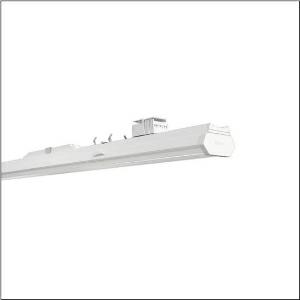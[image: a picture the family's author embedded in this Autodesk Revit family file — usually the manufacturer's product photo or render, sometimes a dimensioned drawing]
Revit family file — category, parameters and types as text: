
# Revit family: licross_r__11_protected_ho_51tp12dn5exm_5ed1
name_source: partatom
category: Lighting Fixtures
units: mm (PartAtom-declared; Revit-internal decimal feet)

## family parameters
Cut with Voids When Loaded = No
Host = Face
Light Source = No
Part Type = Normal
Room Calculation Point = No
Round Connector Dimension = Use Diameter
Shared = No

## types (1)
- --- (1 x LED, 14100 lm, 81.2 W, 5000K)
    Apparent Load = 81 VA
    CIE Flux Codes = 70 91 97 98 100
    Color Rendering = 80
    Color Temperature = 5000K
    Default Elevation = 1800 mm
    Description = Licross® 11 Protected HO, luminaire insert, of sheet steel, galvanised, coil coated, white, length: 1.500mm, width: 90mm, height: 101mm, LED rated luminous flux: 14.100lm, light colour: 850, control gear: DALI 2, with plug, 5-pole, with phase selection, mains connection: 220..240V, AC, 50/60Hz, rated input power: 81W, internal wiring halogen-free, primary optical cover: cover, of PMMA, light emission: direct distribution, primary light characteristic: symmetric, protection rating (complete): IP64, insulation class (complete): insulation class I (protective earthing), certification: CE, ENEC, VDE, UKCA, protection symbol: D if used in an environment with conductive dust loads with corresponding accessories, impact resistance: IK06, permissible ambient temperature for indoor applications: -25..+35°C, corresponds to IFS (International Featured Standards) requirements for safety and quality in the food industry, reducing of maximum allowable ambient temperature of 5°C with ceiling mounting, LABS conformity tested according to VDMA 24364:2018-05, packaging unit: 1 piece
    Height = 92 mm
    Lamp = 1 x LED
    Lamp Light Flux = 14100 lm
    Lamp Power = 81.2 W
    Lamp count = 1
    Length = 1500 mm
    Luminous efficacy = 174 lm/W
    Manufacturer = Siteco
    ModVariant = No
    Model = 51TP12DN5EXM
    Mounting Place = Ceiling
    Mounting Type = Pendant
    Number of Poles = 1
    OnlyDefault = Yes
    Power Factor = 1
    Product Name = Licross® 11 Protected HO
    Product group = luminaire insert | ceiling pendant
    ProductGroupID = 902
    Protection Class = Protection class I
    Protection Degree = IP 64
    RLX_Detail_Level = 1
    RLX_Emergency_Light_Flux = 0 lm
    RLX_Emergency_Type = 0
    RLX_Emergency_Type_DB = No
    RlxData = <blob elided: 24457 chars, md5=e1068099>
    Socket = socket
    Standby Power = 0 W
    System Light Flux = 14100 lm
    System Power = 81 W
    Type Comments = factory setting: luminous flux: 100 % | dim-lin: 254 | 549 mA
    Type Image = l_1256148.jpg
    URL = http://relux.com
    VarID = @adj_018571
    Voltage = 0 V
    Weight = 0.00 kg
    Width = 88 mm

## geometry (parser evidence)
native form markers: Blend x4, Sweep x11
no freeform markers — native parametric forms only
